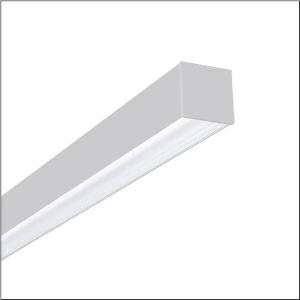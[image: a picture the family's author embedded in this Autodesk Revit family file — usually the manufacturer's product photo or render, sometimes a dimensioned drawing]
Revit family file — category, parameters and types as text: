
# Revit family: silica_r_5mx31bd1w4a_74d2
name_source: partatom
category: Lighting Fixtures
units: mm (PartAtom-declared; Revit-internal decimal feet)

## family parameters
Cut with Voids When Loaded = No
Host = Face
Light Source = No
Part Type = Normal
Room Calculation Point = No
Round Connector Dimension = Use Diameter
Shared = No

## types (1)
- --- (1 x LED, 7070 lm, 45.6 W, 4000K)
    Apparent Load = 46 VA
    CIE Flux Codes = 82 97 100 70 100
    Color Rendering = 80
    Color Temperature = 4000K
    Default Elevation = 1800 mm
    Description = Silica®, office luminaire, of aluminium, light emission: direct/indirect distribution, primary light characteristic: symmetric, installation type: suspended mounting, LED, rated luminous flux: 7.070lm, luminous efficacy: 155lm/W, light colour: 840, colour temperature: 4000K, control gear: ECG DALI, with terminal, 3+2-pole, max. 2.5mm², mains connection: 230V, AC, 50/60Hz, connection cable inclusive, cable length: 1,5m, rated input power: 46W, luminaire housing, of aluminium, traffic white (RAL 9016), length: 1.442mm, width: 65mm, height: 64mm, protection rating (complete): IP20, insulation class (complete): insulation class I (protective earthing), certification: CE, permissible operating ambient temperature: 0..+35°C, standard: EN 50419, packaging unit: 1 piece
    Height = 64 mm
    Lamp = 1 x LED
    Lamp Light Flux = 7070 lm
    Lamp Power = 45.6 W
    Lamp count = 1
    Length = 1442 mm
    Luminous efficacy = 155 lm/W
    Manufacturer = Siteco
    ModVariant = No
    Model = 5MX31BD1W4A
    Mounting Place = Ceiling
    Mounting Type = Pendant
    Number of Poles = 1
    OnlyDefault = Yes
    Power Factor = 1
    Product Name = Silica®
    Product group = office luminaire | ceiling pendant
    ProductGroupID = 902
    Protection Class = Protection class I
    Protection Degree = IP 20
    RLX_Detail_Level = 1
    RLX_Emergency_Light_Flux = 0 lm
    RLX_Emergency_Type = 0
    RLX_Emergency_Type_DB = No
    RlxData = <blob elided: 28857 chars, md5=6bbfa63f>
    Socket = socket
    Standby Power = 0 W
    System Light Flux = 7070 lm
    System Power = 46 W
    Type Comments = factory setting: direct and indirect light
    Type Image = l_1003924.jpg
    URL = http://relux.com
    VarID = @adj_155044
    Voltage = 0 V
    Weight = 0.00 kg
    Width = 66 mm

## geometry (parser evidence)
native form markers: Blend x4, Sweep x14
no freeform markers — native parametric forms only
